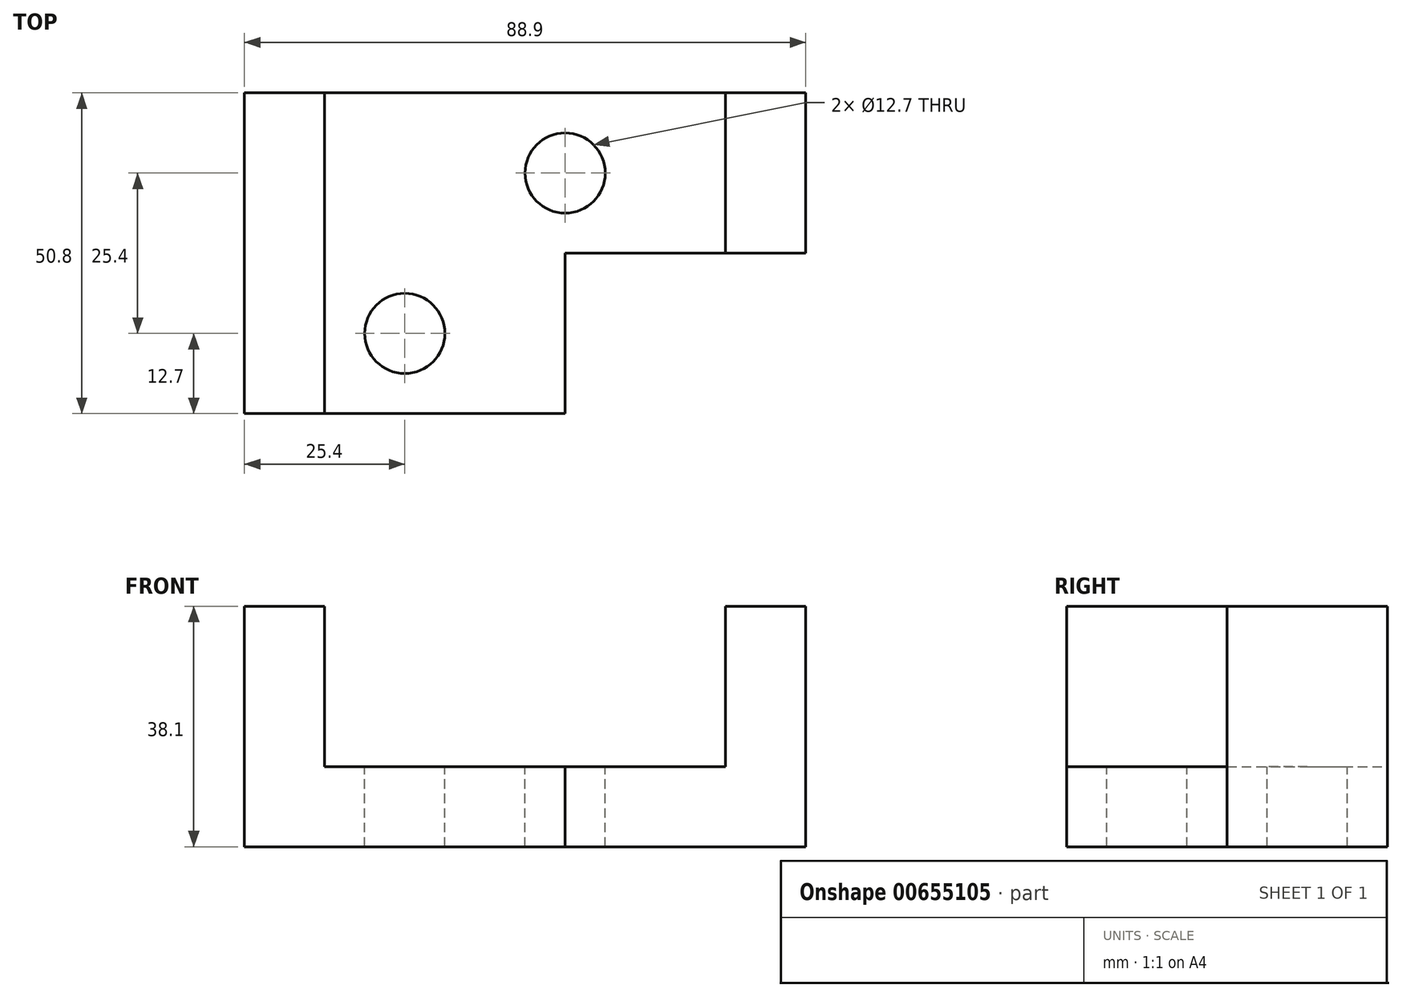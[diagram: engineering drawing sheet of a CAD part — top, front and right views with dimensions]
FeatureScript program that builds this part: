
annotation { "Feature Type Name" : "Feature", "Feature Type Description" : "" }
export const myFeature = defineFeature(function(context is Context, id is Id, definition is map)
    precondition{}
    {
        {
            var Q0;
            Q0=qCreatedBy(makeId("Front.planeOp"),FACE);
            var sketch = newSketch(context, id + "F0", { "sketchPlane" : qUnion([Q0])});
            skLineSegment(sketch, "E0", {"start": v(-88.9, 0) * mm, "end": v(-88.9, -38.1) * mm});
            skLineSegment(sketch, "E1", {"start": v(-88.9, -38.1) * mm, "end": v(0, -38.1) * mm});
            skLineSegment(sketch, "E2", {"start": v(0, -38.1) * mm, "end": v(0, 0) * mm});
            skLineSegment(sketch, "E3", {"start": v(0, 0) * mm, "end": v(-12.7, 0) * mm});
            skLineSegment(sketch, "E4", {"start": v(-12.7, 0) * mm, "end": v(-12.7, -25.4) * mm});
            skLineSegment(sketch, "E5", {"start": v(-12.7, -25.4) * mm, "end": v(-76.2, -25.4) * mm});
            skLineSegment(sketch, "E6", {"start": v(-76.2, -25.4) * mm, "end": v(-76.2, 0) * mm});
            skLineSegment(sketch, "E7", {"start": v(-76.2, 0) * mm, "end": v(-88.9, 0) * mm});
            skSolve(sketch);
        }
        {
            var Q0;
            Q0=makeQuery(id+"F0.imprint","IMPRINT",FACE,{"disambiguationData":[TD([[makeQuery(id+"F0.imprint","IMPRINT",EDGE,{"derivedFrom":sQuery(id+"F0.wireOp",EDGE,"E0")}),1.0]])]});
            extrude(context, id + "F1", {"entities" : qUnion([Q0]), "depth" : 50.8 * mm, "offsetDistance" : 25.4 * mm});
        }
        {
            var Q0;
            Q0=makeQuery(id+"F1.opExtrude","SWEPT_FACE",FACE,{"disambiguationData":[OSD([sQuery(id+"F0.wireOp",EDGE,"E2")])]});
            var sketch = newSketch(context, id + "F2", { "sketchPlane" : qUnion([Q0])});
            skLineSegment(sketch, "E8.bottom", {"start": v(-50.8, 0) * mm, "end": v(-25.4, 0) * mm});
            skLineSegment(sketch, "E8.top", {"start": v(-50.8, -38.1) * mm, "end": v(-25.4, -38.1) * mm});
            skLineSegment(sketch, "E8.left", {"start": v(-50.8, 0) * mm, "end": v(-50.8, -38.1) * mm});
            skLineSegment(sketch, "E8.right", {"start": v(-25.4, 0) * mm, "end": v(-25.4, -38.1) * mm});
            skSolve(sketch);
        }
        {
            var Q0;
            Q0 = qSketchRegion(id + "F2", true);
            extrude(context, id + "F3", {"entities" : qUnion([Q0]), "operationType" : NewBodyOperationType.REMOVE, "oppositeDirection" : true, "depth" : 38.1 * mm, "offsetDistance" : 25.4 * mm});
        }
        {
            var Q0;
            Q0=qCreatedBy(makeId("Top.planeOp"),FACE);
            var sketch = newSketch(context, id + "F4", { "sketchPlane" : qUnion([Q0])});
            skCircle(sketch, "E9", {"center": v(-38.1, -12.7) * mm, "radius": 6.35 * mm});
            skCircle(sketch, "E10", {"center": v(-63.5, -38.1) * mm, "radius": 6.35 * mm});
            skSolve(sketch);
        }
        {
            var Q0;
            Q0=makeQuery(id+"F4.imprint","IMPRINT",FACE,{"disambiguationData":[TD([[makeQuery(id+"F4.imprint","IMPRINT",EDGE,{"derivedFrom":sQuery(id+"F4.wireOp",EDGE,"E10")}),1.0]])]});
            extrude(context, id + "F5", {"entities" : qUnion([Q0]), "operationType" : NewBodyOperationType.REMOVE, "oppositeDirection" : true, "depth" : 12.7 * mm, "offsetDistance" : 25.4 * mm});
        }
        {
            var Q0;
            Q0=makeQuery(id+"F4.imprint","IMPRINT",FACE,{"disambiguationData":[TD([[makeQuery(id+"F4.imprint","IMPRINT",EDGE,{"derivedFrom":sQuery(id+"F4.wireOp",EDGE,"E10")}),1.0]])]});
            extrude(context, id + "F6", {"entities" : qUnion([Q0]), "operationType" : NewBodyOperationType.REMOVE, "endBound" : BoundingType.THROUGH_ALL, "oppositeDirection" : true, "depth" : 12.7 * mm, "offsetDistance" : 25.4 * mm});
        }
        {
            var Q0;
            Q0=makeQuery(id+"F4.imprint","IMPRINT",FACE,{"disambiguationData":[TD([[makeQuery(id+"F4.imprint","IMPRINT",EDGE,{"derivedFrom":sQuery(id+"F4.wireOp",EDGE,"E9")}),1.0]])]});
            extrude(context, id + "F7", {"entities" : qUnion([Q0]), "operationType" : NewBodyOperationType.REMOVE, "endBound" : BoundingType.THROUGH_ALL, "oppositeDirection" : true, "depth" : 12.7 * mm, "offsetDistance" : 25.4 * mm});
        }
    });
